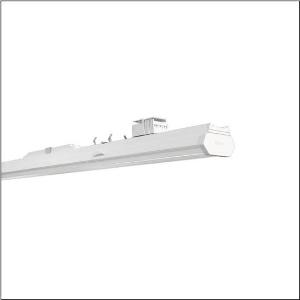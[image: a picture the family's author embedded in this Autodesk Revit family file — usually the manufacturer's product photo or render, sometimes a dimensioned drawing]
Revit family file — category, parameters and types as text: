
# Revit family: licross_r__11_protected_ho_51tp12dn4fxm_edee
name_source: partatom
category: Lighting Fixtures
units: mm (PartAtom-declared; Revit-internal decimal feet)

## family parameters
Cut with Voids When Loaded = No
Host = Face
Light Source = No
Part Type = Normal
Room Calculation Point = No
Round Connector Dimension = Use Diameter
Shared = No

## types (1)
- --- (1 x LED, 15270 lm, 87.3 W, 4000K)
    Apparent Load = 87 VA
    CIE Flux Codes = 70 91 97 98 100
    Color Rendering = 80
    Color Temperature = 4000K
    Default Elevation = 1800 mm
    Description = Licross® 11 Protected HO, luminaire insert, of sheet steel, galvanised, coil coated, white, length: 1.500mm, width: 90mm, height: 101mm, LED rated luminous flux: 15.270lm, light colour: 840, control gear: DALI 2, with plug, 5-pole, with phase selection, mains connection: 220..240V, AC, 50/60Hz, rated input power: 87W, halogen-free wiring, primary optical cover: cover, of PMMA, light emission: direct distribution, primary light characteristic: symmetric, protection rating (complete): IP64, insulation class (complete): insulation class I (protective earthing), certification: CE, ENEC, VDE, UKCA, protection symbol: D if used in an environment with conductive dust loads with corresponding accessories, impact resistance: IK06, permissible ambient temperature for indoor applications: -25..+30°C, corresponds to IFS (International Featured Standards) requirements for safety and quality in the food industry, reducing of maximum allowable ambient temperature of 5°C with ceiling mounting, LABS conformity tested according to VDMA 24364:2018-05, packaging unit: 1 piece
    Height = 92 mm
    Lamp = 1 x LED
    Lamp Light Flux = 15270 lm
    Lamp Power = 87.3 W
    Lamp count = 1
    Length = 1500 mm
    Luminous efficacy = 175 lm/W
    Manufacturer = Siteco
    ModVariant = No
    Model = 51TP12DN4FXM
    Mounting Place = Ceiling
    Mounting Type = Pendant
    Number of Poles = 1
    OnlyDefault = Yes
    Power Factor = 1
    Product Name = Licross® 11 Protected HO
    Product group = luminaire insert
    ProductGroupID = 901
    Protection Class = Protection class I
    Protection Degree = IP 64
    RLX_Detail_Level = 1
    RLX_Emergency_Light_Flux = 0 lm
    RLX_Emergency_Type = 0
    RLX_Emergency_Type_DB = No
    RlxData = <blob elided: 24453 chars, md5=6d505b17>
    Socket = socket
    Standby Power = 0 W
    System Light Flux = 15270 lm
    System Power = 87 W
    Type Comments = factory setting: luminous flux: 100 % | dim-lin: 254 | 491 mA
    Type Image = l_1256148.jpg
    URL = http://relux.com
    VarID = @adj_016331
    Voltage = 0 V
    Weight = 0.00 kg
    Width = 88 mm

## geometry (parser evidence)
native form markers: Blend x4, Sweep x10
no freeform markers — native parametric forms only
